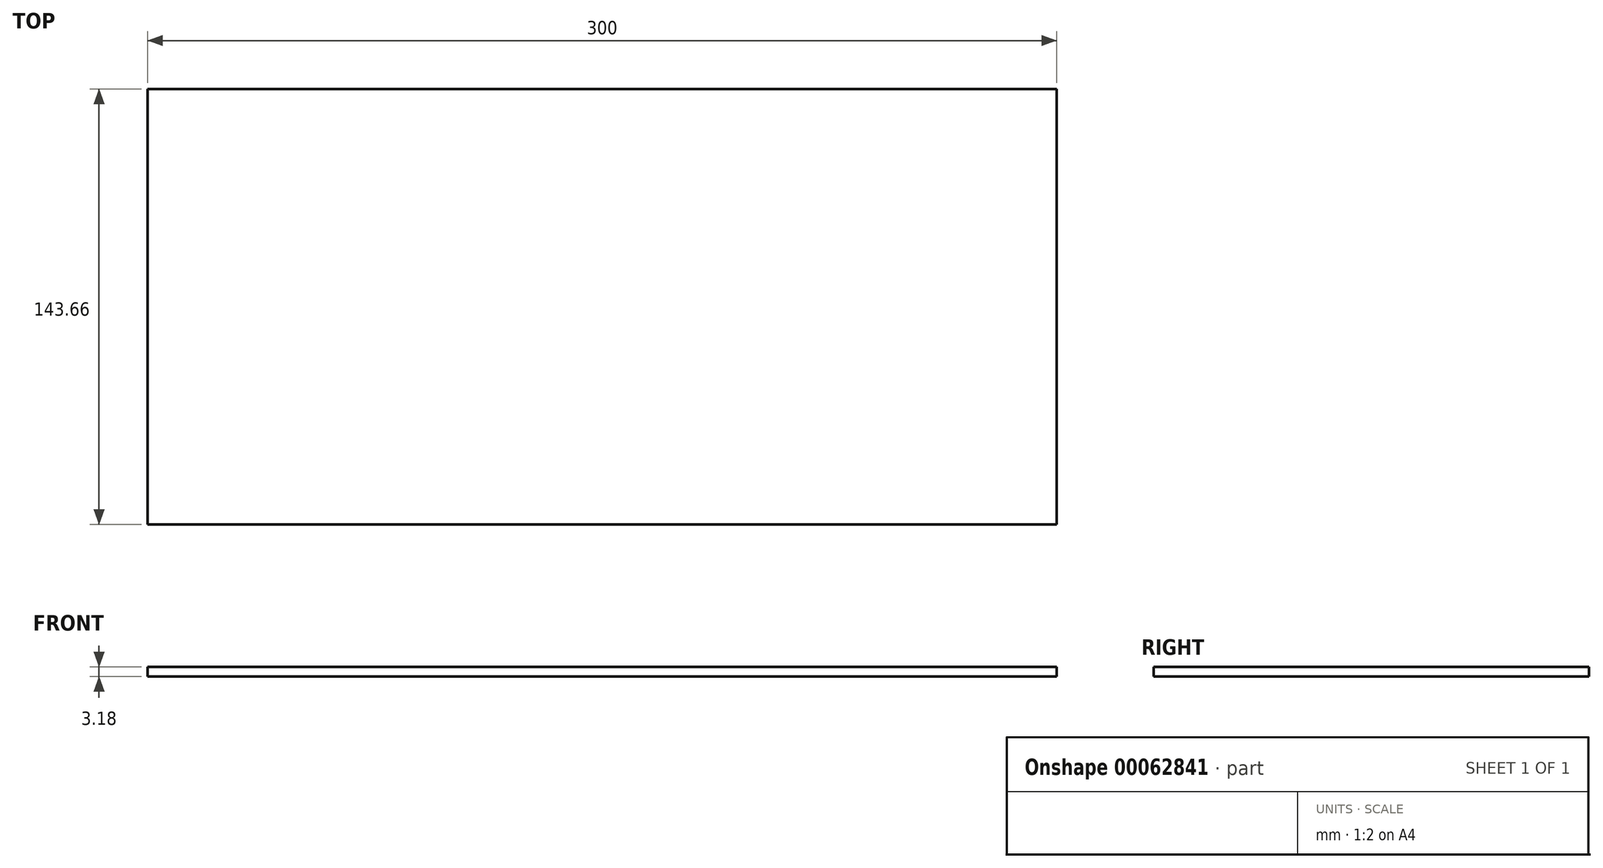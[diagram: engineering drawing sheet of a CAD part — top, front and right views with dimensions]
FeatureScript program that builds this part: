
annotation { "Feature Type Name" : "Feature", "Feature Type Description" : "" }
export const myFeature = defineFeature(function(context is Context, id is Id, definition is map)
    precondition{}
    {
        {
            var Q0;
            Q0=qCreatedBy(makeId("Top.planeOp"),FACE);
            var sketch = newSketch(context, id + "F0", { "sketchPlane" : qUnion([Q0])});
            skLineSegment(sketch, "E0.rect.bottom", {"start": v(-150, 71.82) * mm, "end": v(150, 71.82) * mm});
            skLineSegment(sketch, "E0.rect.top", {"start": v(-150, -71.82) * mm, "end": v(150, -71.82) * mm});
            skLineSegment(sketch, "E0.rect.left", {"start": v(-150, 71.82) * mm, "end": v(-150, -71.82) * mm});
            skLineSegment(sketch, "E0.rect.right", {"start": v(150, 71.82) * mm, "end": v(150, -71.82) * mm});
            skPoint(sketch, "E0.rect.middle", {"position": v(0, 0) * mm});
            skSolve(sketch);
        }
        {
            var Q0;
            Q0=makeQuery(id+"F0.imprint","IMPRINT",FACE,{"disambiguationData":[TD([[makeQuery(id+"F0.imprint","IMPRINT",EDGE,{"derivedFrom":sQuery(id+"F0.wireOp",EDGE,"E0.rect.bottom")}),-1.0]])]});
            extrude(context, id + "F1", {"entities" : qUnion([Q0]), "endBound" : BoundingType.SYMMETRIC, "depth" : 3.17 * mm});
        }
    });
